# Revit family: SH-6157-12pc
name_source: partatom
category: Lighting Fixtures
revit_build: Autodesk Revit 2017 (Build: 20160225_1515(x64)
units: mm (PartAtom-declared; Revit-internal decimal feet)

## family parameters
Always vertical = Yes
Cut with Voids When Loaded = No
Host = Ceiling
Light Source = Yes
OmniClass Number = 23.80.70.11
OmniClass Title = Luminaries for Internal Lighting
Part Type = Normal
Room Calculation Point = No
Round Connector Dimension = Use Diameter
Shared = No

## types (2) — shared parameters
Color Filter = 16777215
Diameter = 32 cm
Dimming Lamp Color Temperature Shift = <None>
Height = 33 cm
IP = X3
Lamp = E27
Manufacturer = SHOA
Model = SH-6157-12pc
Photometric Web File = FLOODLIGHT_LED_5730_100W_CW.IES
Tilt Angle = 90.00°
URL = https://www.shoaco.com
Voltage/Frequency = 230V/50HZ
Website = www.shoaco.com
consumption current = 0 A
instalation Class = Pendant Mounted
wattage. = 0 W

## per-type parameters (varying)
| type | Body color | Reflector Material |
| SH-6157-12pc(Black body-E27) | Black Body | Polycarbonate |
| SH-6157-12pc(White body-E27) | White Body | <By Category> |

## geometry (parser evidence)
native form markers: Sweep x2
no freeform markers — native parametric forms only
